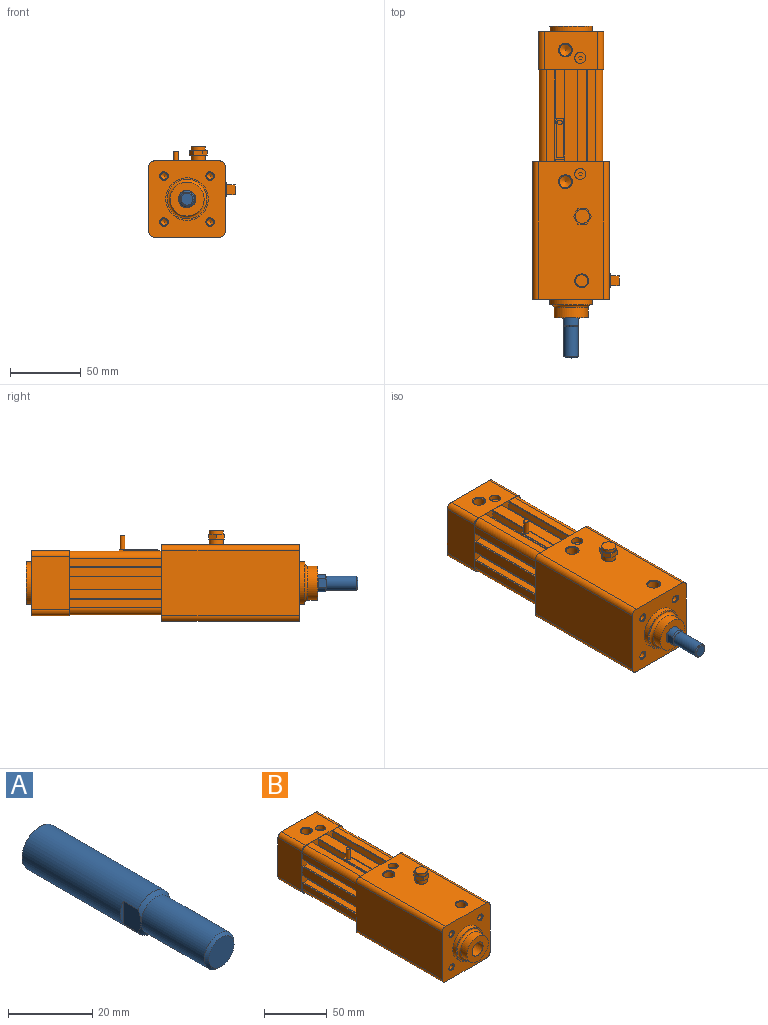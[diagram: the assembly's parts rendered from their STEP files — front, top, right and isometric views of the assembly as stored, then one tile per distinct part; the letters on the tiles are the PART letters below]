
ASSEMBLY  parts=2 mates=1
PART A: 11 faces, bbox 12x61x12 mm
  f0: plane 8.47x8.47mm, normal (0,-1,0), area 56.3mm2, adj f4
  f1: plane 12x12mm, normal (0,1,0), area 113.1mm2, adj f7
  f2: plane 6.63x1mm, normal (0,-1,0), area 4.5mm2, adj f6,f7
  f3: plane 6.63x1mm, normal (0,-1,0), area 4.5mm2, adj f7,f8
  f4: cone r=0mm half-angle=45deg, axis (0,1,0), area 31.5mm2, adj f0,f9
  f5: cone r=0mm half-angle=45deg, axis (0,1,0), area 18.1mm2, adj f6,f7,f8,f9
  f6: plane 6.63x6mm, normal (-1,0,0), area 37.5mm2, adj f2,f5,f7,f10
  f7: cylinder r=6mm len=38mm, axis (0,1,0), area 1362.3mm2, adj f1,f2,f3,f5,f6,f8,f10
  f8: plane 6.63x6mm, normal (1,0,0), area 37.5mm2, adj f3,f5,f7,f10
  f9: cylinder r=5mm len=21.23mm, axis (0,1,0), area 667.1mm2, adj f4,f5,f10
  f10: cone r=0mm half-angle=45deg, axis (0,1,0), area 18.1mm2, adj f6,f7,f8,f9
PART B: 258 faces, bbox 61x206x64 mm
  f0: plane 4.77x4.77mm, normal (0,1,0), area 17.9mm2, adj f5
  f1: plane 4.77x4.77mm, normal (0,1,0), area 17.9mm2, adj f6
  f2: plane 4.77x4.77mm, normal (0,1,0), area 17.9mm2, adj f7
  f3: plane 4.77x4.77mm, normal (0,1,0), area 17.9mm2, adj f8
  f4: plane 12.4x12.4mm, normal (0,-1,0), area 120.8mm2, adj f9
  f5: cylinder r=2.39mm len=12.39mm, axis (0,1,0), area 185.7mm2, adj f0,f10
  f6: cylinder r=2.39mm len=12.39mm, axis (0,-1,0), area 185.7mm2, adj f1,f11
  f7: cylinder r=2.39mm len=12.39mm, axis (0,-1,0), area 185.7mm2, adj f2,f12
  f8: cylinder r=2.39mm len=12.39mm, axis (0,1,0), area 185.7mm2, adj f3,f13
  f9: cylinder r=6.2mm len=27mm, axis (0,-1,0), area 1051.8mm2, adj f4,f15
  f10: cone r=0mm half-angle=45deg, axis (0,1,0), area 14.7mm2, adj f5,f16,f17,f18,f19,f20,f21
  f11: cone r=0mm half-angle=45deg, axis (0,1,0), area 14.7mm2, adj f6,f22,f23,f24,f25,f26,f27
  f12: cone r=0mm half-angle=45deg, axis (0,1,0), area 14.7mm2, adj f7,f28,f29,f30,f31,f32,f33
  f13: cone r=0mm half-angle=45deg, axis (0,1,0), area 14.7mm2, adj f8,f34,f35,f36,f37,f38,f39
  f14: plane 10x10mm, normal (0,0,1), area 78.5mm2, adj f40
  f15: plane 24x24mm, normal (0,-1,0), area 331.6mm2, adj f9,f41
  f16: plane 2.6x1.5mm, normal (0,1,0), area 0.5mm2, adj f10,f42,f43
  f17: plane 3x0.87mm, normal (0,1,0), area 0.5mm2, adj f10,f43,f44
  f18: plane 2.6x1.5mm, normal (0,1,0), area 0.5mm2, adj f10,f44,f45
  f19: plane 2.6x1.5mm, normal (0,1,0), area 0.5mm2, adj f10,f45,f46
  f20: plane 3x0.87mm, normal (0,1,0), area 0.5mm2, adj f10,f46,f47
  f21: plane 2.6x1.5mm, normal (0,1,0), area 0.5mm2, adj f10,f42,f47
  f22: plane 3x0.87mm, normal (0,1,0), area 0.5mm2, adj f11,f48,f49
  f23: plane 2.6x1.5mm, normal (0,1,0), area 0.5mm2, adj f11,f49,f50
  f24: plane 2.6x1.5mm, normal (0,1,0), area 0.5mm2, adj f11,f50,f51
  f25: plane 3x0.87mm, normal (0,1,0), area 0.5mm2, adj f11,f51,f52
  f26: plane 2.6x1.5mm, normal (0,1,0), area 0.5mm2, adj f11,f52,f53
  f27: plane 2.6x1.5mm, normal (0,1,0), area 0.5mm2, adj f11,f48,f53
  f28: plane 3x0.87mm, normal (0,1,0), area 0.5mm2, adj f12,f54,f55
  f29: plane 2.6x1.5mm, normal (0,1,0), area 0.5mm2, adj f12,f55,f56
  f30: plane 2.6x1.5mm, normal (0,1,0), area 0.5mm2, adj f12,f56,f57
  f31: plane 3x0.87mm, normal (0,1,0), area 0.5mm2, adj f12,f57,f58
  f32: plane 2.6x1.5mm, normal (0,1,0), area 0.5mm2, adj f12,f58,f59
  f33: plane 2.6x1.5mm, normal (0,1,0), area 0.5mm2, adj f12,f54,f59
  f34: plane 2.6x1.5mm, normal (0,1,0), area 0.5mm2, adj f13,f60,f61
  f35: plane 3x0.87mm, normal (0,1,0), area 0.5mm2, adj f13,f61,f62
  f36: plane 2.6x1.5mm, normal (0,1,0), area 0.5mm2, adj f13,f62,f63
  f37: plane 2.6x1.5mm, normal (0,1,0), area 0.5mm2, adj f13,f63,f64
  f38: plane 3x0.87mm, normal (0,1,0), area 0.5mm2, adj f13,f64,f65
  f39: plane 2.6x1.5mm, normal (0,1,0), area 0.5mm2, adj f13,f60,f65
  f40: cylinder r=5mm len=10mm, axis (0,0,1), area 78.5mm2, adj f14,f67
  f41: cylinder r=12mm len=24mm, axis (0,1,0), area 527.8mm2, adj f15,f70
  f42: plane 3.46x3mm, normal (-1,0,0), area 10.4mm2, adj f16,f21,f43,f47,f76
  f43: plane 3x3mm, normal (-0.5,0,-0.87), area 10.4mm2, adj f16,f17,f42,f44,f76
  f44: plane 3x3mm, normal (0.5,0,-0.87), area 10.4mm2, adj f17,f18,f43,f45,f76
  f45: plane 3.46x3mm, normal (1,0,0), area 10.4mm2, adj f18,f19,f44,f46,f76
  f46: plane 3x3mm, normal (0.5,0,0.87), area 10.4mm2, adj f19,f20,f45,f47,f76
  f47: plane 3x3mm, normal (-0.5,0,0.87), area 10.4mm2, adj f20,f21,f42,f46,f76
  f48: plane 3x3mm, normal (0.5,0,0.87), area 10.4mm2, adj f22,f27,f49,f53,f77
  f49: plane 3x3mm, normal (-0.5,0,0.87), area 10.4mm2, adj f22,f23,f48,f50,f77
  f50: plane 3.46x3mm, normal (-1,0,0), area 10.4mm2, adj f23,f24,f49,f51,f77
  f51: plane 3x3mm, normal (-0.5,0,-0.87), area 10.4mm2, adj f24,f25,f50,f52,f77
  f52: plane 3x3mm, normal (0.5,0,-0.87), area 10.4mm2, adj f25,f26,f51,f53,f77
  f53: plane 3.46x3mm, normal (1,0,0), area 10.4mm2, adj f26,f27,f48,f52,f77
  f54: plane 3x3mm, normal (0.5,0,0.87), area 10.4mm2, adj f28,f33,f55,f59,f78
  f55: plane 3x3mm, normal (-0.5,0,0.87), area 10.4mm2, adj f28,f29,f54,f56,f78
  f56: plane 3.46x3mm, normal (-1,0,0), area 10.4mm2, adj f29,f30,f55,f57,f78
  f57: plane 3x3mm, normal (-0.5,0,-0.87), area 10.4mm2, adj f30,f31,f56,f58,f78
  f58: plane 3x3mm, normal (0.5,0,-0.87), area 10.4mm2, adj f31,f32,f57,f59,f78
  f59: plane 3.46x3mm, normal (1,0,0), area 10.4mm2, adj f32,f33,f54,f58,f78
  f60: plane 3.46x3mm, normal (-1,0,0), area 10.4mm2, adj f34,f39,f61,f65,f79
  f61: plane 3x3mm, normal (-0.5,0,-0.87), area 10.4mm2, adj f34,f35,f60,f62,f79
  f62: plane 3x3mm, normal (0.5,0,-0.87), area 10.4mm2, adj f35,f36,f61,f63,f79
  f63: plane 3.46x3mm, normal (1,0,0), area 10.4mm2, adj f36,f37,f62,f64,f79
  f64: plane 3x3mm, normal (0.5,0,0.87), area 10.4mm2, adj f37,f38,f63,f65,f79
  f65: plane 3x3mm, normal (-0.5,0,0.87), area 10.4mm2, adj f38,f39,f60,f64,f79
  f66: plane 2.89x2.5mm, normal (0,0,1), area 5.4mm2, adj f80,f81,f82,f83,f84,f85
  f67: plane 12.7x11mm, normal (0,0,1), area 26.2mm2, adj f40,f88,f89,f90,f91,f92,f93
  f68: plane 2.89x2.5mm, normal (0,0,1), area 5.4mm2, adj f94,f95,f96,f97,f98,f99
  f69: plane 7x7mm, normal (1,0,0), area 49mm2, adj f101,f102,f103,f104
  f70: torus R=14mm, axis (0,1,0), area 251.2mm2, adj f41,f105
  f71: cone r=0mm half-angle=60deg, axis (0,-1,0), area 20.7mm2, adj f106
  f72: cone r=0mm half-angle=60deg, axis (0,-1,0), area 20.7mm2, adj f107
  f73: cone r=0mm half-angle=60deg, axis (0,-1,0), area 20.7mm2, adj f108
  f74: cone r=0mm half-angle=60deg, axis (0,-1,0), area 20.7mm2, adj f109
  f75: plane 30x30mm, normal (0,1,0), area 706.9mm2, adj f110
  f76: plane 9x9mm, normal (0,1,0), area 32.4mm2, adj f42,f43,f44,f45,f46,f47,f111
  f77: plane 9x9mm, normal (0,1,0), area 32.4mm2, adj f48,f49,f50,f51,f52,f53,f112
  f78: plane 9x9mm, normal (0,1,0), area 32.4mm2, adj f54,f55,f56,f57,f58,f59,f113
  f79: plane 9x9mm, normal (0,1,0), area 32.4mm2, adj f60,f61,f62,f63,f64,f65,f114
  f80: plane 8.13x1.44mm, normal (0,-1,0), area 11.7mm2, adj f66,f81,f85,f115
  f81: plane 8.13x1.25mm, normal (-0.87,-0.5,0), area 11.7mm2, adj f66,f80,f82,f115
  f82: plane 8.13x1.25mm, normal (-0.87,0.5,0), area 11.7mm2, adj f66,f81,f83,f115
  f83: plane 8.13x1.44mm, normal (0,1,0), area 11.7mm2, adj f66,f82,f84,f115
  f84: plane 8.13x1.25mm, normal (0.87,0.5,0), area 11.7mm2, adj f66,f83,f85,f115
  f85: plane 8.13x1.25mm, normal (0.87,-0.5,0), area 11.7mm2, adj f66,f80,f84,f115
  f86: cone r=0mm half-angle=60deg, axis (0,0,1), area 66.5mm2, adj f116
  f87: plane 8.57x8.57mm, normal (0,0,1), area 57.7mm2, adj f117
  f88: plane 5.5x3.5mm, normal (-0.87,0.5,0), area 22.2mm2, adj f67,f89,f93,f118
  f89: plane 6.35x3.5mm, normal (0,1,0), area 22.2mm2, adj f67,f88,f90,f118
  f90: plane 5.5x3.5mm, normal (0.87,0.5,0), area 22.2mm2, adj f67,f89,f91,f118
  f91: plane 5.5x3.5mm, normal (0.87,-0.5,0), area 22.2mm2, adj f67,f90,f92,f118
  f92: plane 6.35x3.5mm, normal (0,-1,0), area 22.2mm2, adj f67,f91,f93,f118
  f93: plane 5.5x3.5mm, normal (-0.87,-0.5,0), area 22.2mm2, adj f67,f88,f92,f118
  f94: plane 8.13x1.44mm, normal (0,-1,0), area 11.7mm2, adj f68,f95,f99,f119
  f95: plane 8.13x1.25mm, normal (-0.87,-0.5,0), area 11.7mm2, adj f68,f94,f96,f119
  f96: plane 8.13x1.25mm, normal (-0.87,0.5,0), area 11.7mm2, adj f68,f95,f97,f119
  f97: plane 8.13x1.44mm, normal (0,1,0), area 11.7mm2, adj f68,f96,f98,f119
  f98: plane 8.13x1.25mm, normal (0.87,0.5,0), area 11.7mm2, adj f68,f97,f99,f119
  f99: plane 8.13x1.25mm, normal (0.87,-0.5,0), area 11.7mm2, adj f68,f94,f98,f119
  f100: cone r=0mm half-angle=60deg, axis (0,0,1), area 66.5mm2, adj f120
  f101: plane 7x6mm, normal (0,-1,0), area 42mm2, adj f69,f102,f104,f121
  f102: plane 7x6mm, normal (0,0,1), area 42mm2, adj f69,f101,f103,f121
  f103: plane 7x6mm, normal (0,1,0), area 42mm2, adj f69,f102,f104,f121
  f104: plane 7x6mm, normal (0,0,-1), area 42mm2, adj f69,f101,f103,f121
  f105: plane 30x30mm, normal (0,-1,0), area 91.1mm2, adj f70,f122
  f106: cylinder r=2.39mm len=18.39mm, axis (0,1,0), area 275.7mm2, adj f71,f123
  f107: cylinder r=2.39mm len=18.39mm, axis (0,-1,0), area 275.7mm2, adj f72,f124
  f108: cylinder r=2.39mm len=18.39mm, axis (0,1,0), area 275.7mm2, adj f73,f125
  f109: cylinder r=2.39mm len=18.39mm, axis (0,-1,0), area 275.7mm2, adj f74,f126
  f110: cylinder r=15mm len=30mm, axis (0,-1,0), area 377mm2, adj f75,f128
  f111: cylinder r=4.5mm len=9mm, axis (0,1,0), area 28.3mm2, adj f76,f128
  f112: cylinder r=4.5mm len=9mm, axis (0,-1,0), area 28.3mm2, adj f77,f128
  f113: cylinder r=4.5mm len=9mm, axis (0,-1,0), area 28.3mm2, adj f78,f128
  f114: cylinder r=4.5mm len=9mm, axis (0,1,0), area 28.3mm2, adj f79,f128
  f115: plane 7.8x7.8mm, normal (0,0,1), area 42.4mm2, adj f80,f81,f82,f83,f84,f85,f129
  f116: cylinder r=4.28mm len=10.52mm, axis (0,0,-1), area 283.2mm2, adj f86,f130
  f117: cylinder r=4.29mm len=9.15mm, axis (0,0,1), area 246.3mm2, adj f87,f131
  f118: plane 12.7x11mm, normal (0,0,-1), area 26.2mm2, adj f88,f89,f90,f91,f92,f93,f132
  f119: plane 7.8x7.8mm, normal (0,0,1), area 42.4mm2, adj f94,f95,f96,f97,f98,f99,f133
  f120: cylinder r=4.28mm len=14.35mm, axis (0,0,-1), area 386.3mm2, adj f100,f134
  f121: plane 9.9x9.9mm, normal (1,0,0), area 28mm2, adj f101,f102,f103,f104,f135
  f122: cylinder r=15mm len=30mm, axis (0,1,0), area 377mm2, adj f105,f136
  f123: cone r=0mm half-angle=45deg, axis (0,-1,0), area 14.7mm2, adj f106,f136
  f124: cone r=0mm half-angle=45deg, axis (0,-1,0), area 14.7mm2, adj f107,f136
  f125: cone r=0mm half-angle=45deg, axis (0,-1,0), area 14.7mm2, adj f108,f136
  f126: cone r=0mm half-angle=45deg, axis (0,-1,0), area 14.7mm2, adj f109,f136
  f127: plane 3.4x3.4mm, normal (0,0,1), area 9.1mm2, adj f137
  f128: plane 46x46mm, normal (0,1,0), area 1140.9mm2, adj f110,f111,f112,f113,f114,f138,f139,f140
  f129: cylinder r=3.9mm len=7.8mm, axis (0,0,-1), area 95.6mm2, adj f115,f145
  f130: cone r=0mm half-angle=45deg, axis (0,0,1), area 23.6mm2, adj f116,f145
  f131: cone r=0mm half-angle=45deg, axis (0,0,1), area 23.6mm2, adj f117,f149
  f132: cylinder r=5mm len=10mm, axis (0,0,1), area 125.7mm2, adj f118,f149
  f133: cylinder r=3.9mm len=7.8mm, axis (0,0,-1), area 95.6mm2, adj f119,f149
  f134: cone r=0mm half-angle=45deg, axis (0,0,1), area 23.6mm2, adj f120,f149
  f135: cylinder r=4.95mm len=9.9mm, axis (-1,0,0), area 31.1mm2, adj f121,f151
  f136: plane 54x54mm, normal (0,-1,0), area 2082.3mm2, adj f122,f123,f124,f125,f126,f148,f149,f150
  f137: cylinder r=1.7mm len=10mm, axis (0,0,-1), area 106.8mm2, adj f127,f234
  f138: cylinder r=4mm len=27mm, axis (0,1,0), area 169.6mm2, adj f128,f139,f145,f240
  f139: plane 38x27mm, normal (-1,0,0), area 1026mm2, adj f128,f138,f140,f240
  f140: cylinder r=4mm len=27mm, axis (0,1,0), area 169.6mm2, adj f128,f139,f141,f240
  f141: plane 38x27mm, normal (0,0,-1), area 1026mm2, adj f128,f140,f142,f240
  f142: cylinder r=4mm len=27mm, axis (0,1,0), area 169.6mm2, adj f128,f141,f143,f240
  f143: plane 38x27mm, normal (1,0,0), area 1026mm2, adj f128,f142,f144,f240
  f144: cylinder r=4mm len=27mm, axis (0,1,0), area 169.6mm2, adj f128,f143,f145,f240
  f145: plane 38x27mm, normal (0,0,1), area 903.9mm2, adj f128,f129,f130,f138,f144,f240
  f146: plane 38x1.11mm, normal (1,0,0), area 42.1mm2, adj f147,f211,f237,f240
  f147: plane 38x0.68mm, normal (0.5,0,-0.87), area 29.9mm2, adj f146,f221,f237,f240
  f148: cylinder r=4mm len=97mm, axis (0,-1,0), area 609.5mm2, adj f136,f149,f155,f242
  f149: plane 97x46mm, normal (0,0,1), area 4187mm2, adj f131,f132,f133,f134,f136,f148,f150,f242
  f150: cylinder r=4mm len=97mm, axis (0,-1,0), area 609.5mm2, adj f136,f149,f151,f242
  f151: plane 97x46mm, normal (1,0,0), area 4385mm2, adj f135,f136,f150,f152,f242
  f152: cylinder r=4mm len=97mm, axis (0,-1,0), area 609.5mm2, adj f136,f151,f153,f242
  f153: plane 97x46mm, normal (0,0,-1), area 4462mm2, adj f136,f152,f154,f242
  f154: cylinder r=4mm len=97mm, axis (0,-1,0), area 609.5mm2, adj f136,f153,f155,f242
  f155: plane 97x46mm, normal (-1,0,0), area 4462mm2, adj f136,f148,f154,f242
  f156: plane 65x1.11mm, normal (0,0,1), area 72mm2, adj f157,f219,f240,f242
  f157: plane 65x8.65mm, normal (-1,0,0), area 562.2mm2, adj f156,f158,f240,f242
  f158: plane 65x1.11mm, normal (0,0,-1), area 72mm2, adj f157,f159,f240,f242
  f159: plane 65x0.68mm, normal (0.87,0,-0.5), area 51.1mm2, adj f158,f160,f240,f242
  f160: plane 65x4.5mm, normal (-0.26,0,-0.97), area 302.8mm2, adj f159,f161,f240,f242
  f161: plane 65x6.3mm, normal (-1,0,0), area 409.5mm2, adj f160,f162,f240,f242
  f162: plane 65x4.5mm, normal (-0.26,0,0.97), area 302.8mm2, adj f161,f163,f240,f242
  f163: plane 65x0.68mm, normal (0.87,0,0.5), area 51.1mm2, adj f162,f164,f240,f242
  f164: plane 65x1.11mm, normal (0,0,1), area 72mm2, adj f163,f165,f240,f242
  f165: plane 65x5.83mm, normal (-1,0,0), area 378.6mm2, adj f164,f166,f240,f242
  f166: cylinder r=5mm len=65mm, axis (0,1,0), area 510.5mm2, adj f165,f167,f240,f242
  f167: plane 65x5.83mm, normal (0,0,-1), area 378.6mm2, adj f166,f168,f240,f242
  f168: plane 65x1.11mm, normal (1,0,0), area 72mm2, adj f167,f169,f240,f242
  f169: plane 65x0.68mm, normal (0.5,0,0.87), area 51.1mm2, adj f168,f170,f240,f242
  f170: plane 65x4.5mm, normal (0.97,0,-0.26), area 302.8mm2, adj f169,f171,f240,f242
  f171: plane 65x6.3mm, normal (0,0,-1), area 409.5mm2, adj f170,f172,f240,f242
  f172: plane 65x4.5mm, normal (-0.97,0,-0.26), area 302.8mm2, adj f171,f173,f240,f242
  f173: plane 65x0.68mm, normal (-0.5,0,0.87), area 51.1mm2, adj f172,f174,f240,f242
  f174: plane 65x1.11mm, normal (-1,0,0), area 72mm2, adj f173,f175,f240,f242
  f175: plane 65x8.65mm, normal (0,0,-1), area 562.2mm2, adj f174,f176,f240,f242
  f176: plane 65x1.11mm, normal (1,0,0), area 72mm2, adj f175,f177,f240,f242
  f177: plane 65x0.68mm, normal (0.5,0,0.87), area 51.1mm2, adj f176,f178,f240,f242
  f178: plane 65x4.5mm, normal (0.97,0,-0.26), area 302.8mm2, adj f177,f179,f240,f242
  f179: plane 65x6.3mm, normal (0,0,-1), area 409.5mm2, adj f178,f180,f240,f242
  f180: plane 65x4.5mm, normal (-0.97,0,-0.26), area 302.8mm2, adj f179,f181,f240,f242
  f181: plane 65x0.68mm, normal (-0.5,0,0.87), area 51.1mm2, adj f180,f182,f240,f242
  f182: plane 65x1.11mm, normal (-1,0,0), area 72mm2, adj f181,f183,f240,f242
  f183: plane 65x5.83mm, normal (0,0,-1), area 378.6mm2, adj f182,f184,f240,f242
  f184: cylinder r=5mm len=65mm, axis (0,1,0), area 510.5mm2, adj f183,f185,f240,f242
  f185: plane 65x5.83mm, normal (1,0,0), area 378.6mm2, adj f184,f186,f240,f242
  f186: plane 65x1.11mm, normal (0,0,1), area 72mm2, adj f185,f187,f240,f242
  f187: plane 65x0.68mm, normal (-0.87,0,0.5), area 51.1mm2, adj f186,f188,f240,f242
  f188: plane 65x4.5mm, normal (0.26,0,0.97), area 302.8mm2, adj f187,f189,f240,f242
  f189: plane 65x6.3mm, normal (1,0,0), area 409.5mm2, adj f188,f190,f240,f242
  f190: plane 65x4.5mm, normal (0.26,0,-0.97), area 302.8mm2, adj f189,f191,f240,f242
  f191: plane 65x0.68mm, normal (-0.87,0,-0.5), area 51.1mm2, adj f190,f192,f240,f242
  f192: plane 65x1.11mm, normal (0,0,-1), area 72mm2, adj f191,f193,f240,f242
  f193: plane 65x8.65mm, normal (1,0,0), area 562.2mm2, adj f192,f194,f240,f242
  f194: plane 65x1.11mm, normal (0,0,1), area 72mm2, adj f193,f195,f240,f242
  f195: plane 65x0.68mm, normal (-0.87,0,0.5), area 51.1mm2, adj f194,f196,f240,f242
  f196: plane 65x4.5mm, normal (0.26,0,0.97), area 302.8mm2, adj f195,f197,f240,f242
  f197: plane 65x6.3mm, normal (1,0,0), area 409.5mm2, adj f196,f198,f240,f242
  f198: plane 65x4.5mm, normal (0.26,0,-0.97), area 302.8mm2, adj f197,f199,f240,f242
  f199: plane 65x0.68mm, normal (-0.87,0,-0.5), area 51.1mm2, adj f198,f200,f240,f242
  f200: plane 65x1.11mm, normal (0,0,-1), area 72mm2, adj f199,f201,f240,f242
  f201: plane 65x5.83mm, normal (1,0,0), area 378.6mm2, adj f200,f202,f240,f242
  f202: cylinder r=5mm len=65mm, axis (0,1,0), area 510.5mm2, adj f201,f203,f240,f242
  f203: plane 65x5.83mm, normal (0,0,1), area 378.6mm2, adj f202,f204,f240,f242
  f204: plane 65x1.11mm, normal (-1,0,0), area 72mm2, adj f203,f205,f240,f242
  f205: plane 65x0.68mm, normal (-0.5,0,-0.87), area 51.1mm2, adj f204,f206,f240,f242
  f206: plane 65x4.5mm, normal (-0.97,0,0.26), area 302.8mm2, adj f205,f207,f240,f242
  f207: plane 65x6.3mm, normal (0,0,1), area 409.5mm2, adj f206,f208,f240,f242
  f208: plane 65x4.5mm, normal (0.97,0,0.26), area 302.8mm2, adj f207,f209,f240,f242
  f209: plane 65x0.68mm, normal (0.5,0,-0.87), area 51.1mm2, adj f208,f210,f240,f242
  f210: plane 65x1.11mm, normal (1,0,0), area 72mm2, adj f209,f239,f240,f242
  f211: plane 65x5.83mm, normal (0,0,1), area 378.6mm2, adj f146,f212,f228,f238,f240,f242
  f212: cylinder r=5mm len=65mm, axis (0,1,0), area 510.5mm2, adj f211,f213,f240,f242
  f213: plane 65x5.83mm, normal (-1,0,0), area 378.6mm2, adj f212,f214,f240,f242
  f214: plane 65x1.11mm, normal (0,0,-1), area 72mm2, adj f213,f215,f240,f242
  f215: plane 65x0.68mm, normal (0.87,0,-0.5), area 51.1mm2, adj f214,f216,f240,f242
  f216: plane 65x4.5mm, normal (-0.26,0,-0.97), area 302.8mm2, adj f215,f217,f240,f242
  f217: plane 65x6.3mm, normal (-1,0,0), area 409.5mm2, adj f216,f218,f240,f242
  f218: plane 65x4.5mm, normal (-0.26,0,0.97), area 302.8mm2, adj f217,f219,f240,f242
  f219: plane 65x0.68mm, normal (0.87,0,0.5), area 51.1mm2, adj f156,f218,f240,f242
  f220: plane 2x0.68mm, normal (0.5,0,-0.87), area 1.6mm2, adj f221,f228,f242,f244
  f221: plane 65x4.5mm, normal (0.97,0,0.26), area 222.6mm2, adj f147,f220,f222,f237,f240,f241,f242,f244
  f222: plane 25x0.43mm, normal (0,0,-1), area 10.6mm2, adj f221,f231,f237,f244
  f223: plane 1x0.55mm, normal (0,0,-1), area 0.6mm2, adj f224,f230,f231,f244
  f224: plane 1.1x1mm, normal (1,0,0), area 1.1mm2, adj f223,f225,f230,f244
  f225: plane 5.1x1mm, normal (0,0,-1), area 5.1mm2, adj f224,f226,f230,f244
  f226: plane 1.1x1mm, normal (-1,0,0), area 1.1mm2, adj f225,f229,f230,f244
  f227: plane 2x1.11mm, normal (-1,0,0), area 2.2mm2, adj f239,f242,f243,f244
  f228: plane 2x1.11mm, normal (1,0,0), area 2.2mm2, adj f211,f220,f242,f244
  f229: plane 1x0.55mm, normal (0,0,-1), area 0.6mm2, adj f226,f230,f244,f245
  f230: plane 6.2x4mm, normal (0,-1,0), area 23.6mm2, adj f223,f224,f225,f226,f229,f231,f245,f246
  f231: plane 25x3mm, normal (1,0,0), area 5.4mm2, adj f222,f223,f230,f237,f244,f246
  f232: plane 3.3x0.55mm, normal (0,0,1), area 1.8mm2, adj f233,f236,f237,f247
  f233: plane 3.3x2.9mm, normal (-1,0,0), area 9.6mm2, adj f232,f237,f246,f247
  f234: plane 27.3x5.1mm, normal (0,0,1), area 130.2mm2, adj f137,f235,f236,f247,f248
  f235: plane 5.1x0.5mm, normal (0,-1,0), area 2.6mm2, adj f234,f236,f248,f249
  f236: plane 27.3x2.6mm, normal (-1,0,0), area 20.6mm2, adj f232,f234,f235,f237,f247,f249
  f237: plane 5.1x1.81mm, normal (0,1,0), area 5mm2, adj f146,f147,f221,f222,f231,f232,f233,f236
  f238: plane 25x0.5mm, normal (-1,0,0), area 12.5mm2, adj f211,f237,f244,f249
  f239: plane 65x8.65mm, normal (0,0,1), area 562.2mm2, adj f210,f227,f240,f242,f250,f251
  f240: plane 46x46mm, normal (0,-1,0), area 459.3mm2, adj f138,f139,f140,f141,f142,f143,f144,f145
  f241: plane 65x6.3mm, normal (0,0,1), area 409.5mm2, adj f221,f240,f242,f253
  f242: plane 54x54mm, normal (0,1,0), area 1259.3mm2, adj f148,f149,f150,f151,f152,f153,f154,f155
  f243: plane 2x0.68mm, normal (-0.5,0,-0.87), area 1.6mm2, adj f227,f242,f244,f253
  f244: plane 8.71x5.1mm, normal (0,-1,0), area 15.2mm2, adj f220,f221,f222,f223,f224,f225,f226,f227
  f245: plane 25x3mm, normal (-1,0,0), area 5.4mm2, adj f229,f230,f244,f246,f254,f257
  f246: plane 27.3x6.2mm, normal (0,0,-1), area 169.3mm2, adj f230,f231,f233,f245,f247,f255
  f247: plane 6.2x5.5mm, normal (0,1,0), area 31.2mm2, adj f232,f233,f234,f236,f246,f248,f255,f256
  f248: plane 27.3x2.6mm, normal (1,0,0), area 20.6mm2, adj f234,f235,f247,f249,f256,f257
  f249: plane 25x7.35mm, normal (0,0,1), area 61.4mm2, adj f235,f236,f237,f238,f244,f248,f250,f257
  f250: plane 25x0.5mm, normal (1,0,0), area 12.5mm2, adj f239,f244,f249,f257
  f251: plane 38x1.11mm, normal (-1,0,0), area 42.1mm2, adj f239,f240,f252,f257
  f252: plane 38x0.68mm, normal (-0.5,0,-0.87), area 29.9mm2, adj f240,f251,f253,f257
  f253: plane 65x4.5mm, normal (-0.97,0,0.26), area 222.6mm2, adj f240,f241,f242,f243,f244,f252,f254,f257
  f254: plane 25x0.43mm, normal (0,0,-1), area 10.6mm2, adj f244,f245,f253,f257
  f255: plane 3.3x2.9mm, normal (1,0,0), area 9.6mm2, adj f246,f247,f256,f257
  f256: plane 3.3x0.55mm, normal (0,0,1), area 1.8mm2, adj f247,f248,f255,f257
  f257: plane 5.1x1.81mm, normal (0,1,0), area 5mm2, adj f245,f248,f249,f250,f251,f252,f253,f254
PLACE A t=(-14.8,6.38,15.57)mm
PLACE B t=(-14.8,-0.12,15.57)mm
MATE cylindrical A.f4 <-> B.f9  axis (0,1,0) through (-14.8,0.38,15.57)mm
